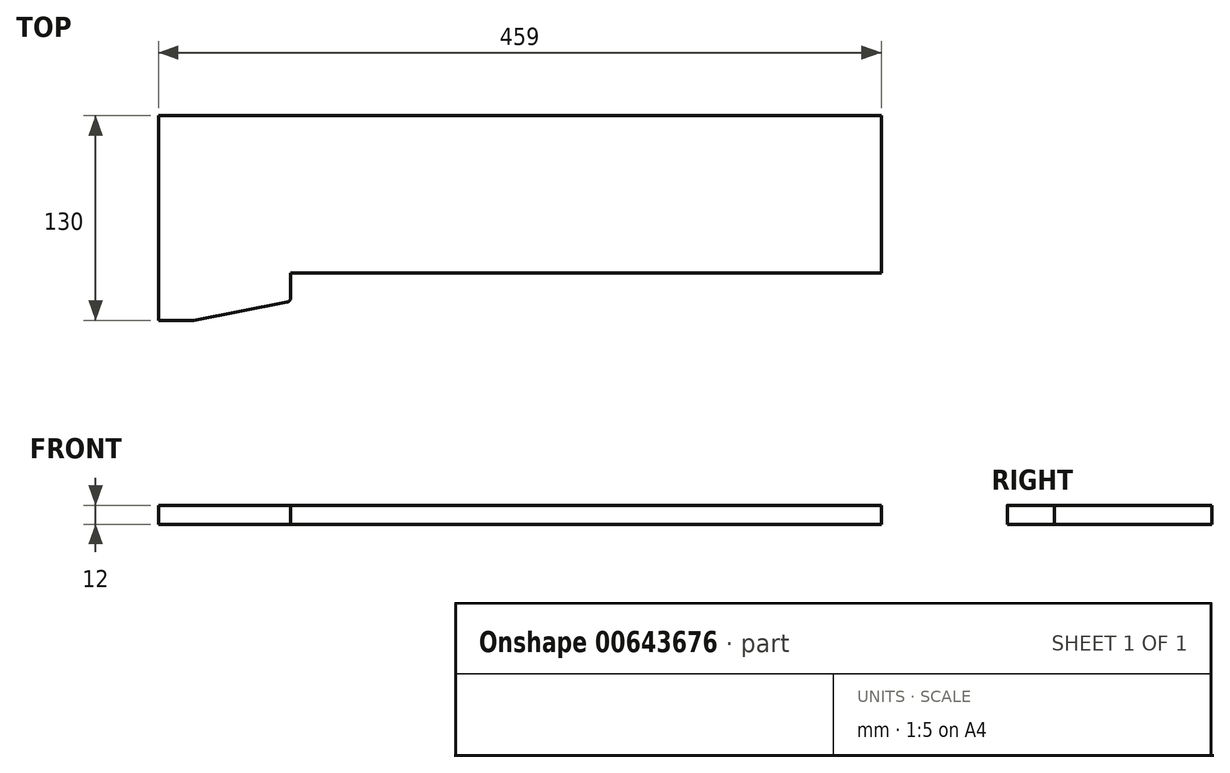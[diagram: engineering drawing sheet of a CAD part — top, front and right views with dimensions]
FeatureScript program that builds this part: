
annotation { "Feature Type Name" : "Feature", "Feature Type Description" : "" }
export const myFeature = defineFeature(function(context is Context, id is Id, definition is map)
    precondition{}
    {
        {
            var Q0;
            Q0=qCreatedBy(makeId("Top.planeOp"),FACE);
            var sketch = newSketch(context, id + "F0", { "sketchPlane" : qUnion([Q0])});
            skLineSegment(sketch, "E0.bottom", {"start": v(-207.5, 0) * mm, "end": v(-229.5, 0) * mm});
            skLineSegment(sketch, "E0.top", {"start": v(229.5, 130) * mm, "end": v(-229.5, 130) * mm});
            skLineSegment(sketch, "E0.left", {"start": v(229.5, 30) * mm, "end": v(229.5, 130) * mm});
            skLineSegment(sketch, "E0.right", {"start": v(-229.5, 0) * mm, "end": v(-229.5, 130) * mm});
            skPoint(sketch, "E0.middle", {"position": v(0, 65) * mm});
            skLineSegment(sketch, "E1", {"start": v(229.5, 30) * mm, "end": v(-145.5, 30) * mm});
            skLineSegment(sketch, "E2", {"start": v(-145.5, 30) * mm, "end": v(-145.5, 12) * mm});
            skLineSegment(sketch, "E3", {"start": v(-145.5, 12) * mm, "end": v(-207.5, 0) * mm});
            skPoint(sketch, "E4.orphan", {"position": v(229.5, 0) * mm});
            skSolve(sketch);
        }
        {
            var Q0;
            Q0 = qSketchRegion(id + "F0", true);
            extrude(context, id + "F1", {"entities" : qUnion([Q0]), "depth" : 12 * mm, "offsetDistance" : 25 * mm});
        }
        {
            var Q0;
            Q0=makeQuery(id+"F1.opExtrude","SWEPT_EDGE",EDGE,{"disambiguationData":[OSD([sQuery(id+"F0.wireOp",EDGE,"E2"),sQuery(id+"F0.wireOp",EDGE,"E3")])]});
            var Q1;
            Q1=makeQuery(id+"F1.opExtrude","SWEPT_EDGE",EDGE,{"disambiguationData":[OSD([sQuery(id+"F0.wireOp",EDGE,"E0.bottom"),sQuery(id+"F0.wireOp",EDGE,"E3")])]});
            fillet(context, id + "F2", {"entities" : qUnion([Q0, Q1]), "radius" : 3 * mm, "tangentPropagation" : true, "allowEdgeOverflow" : false});
        }
    });
